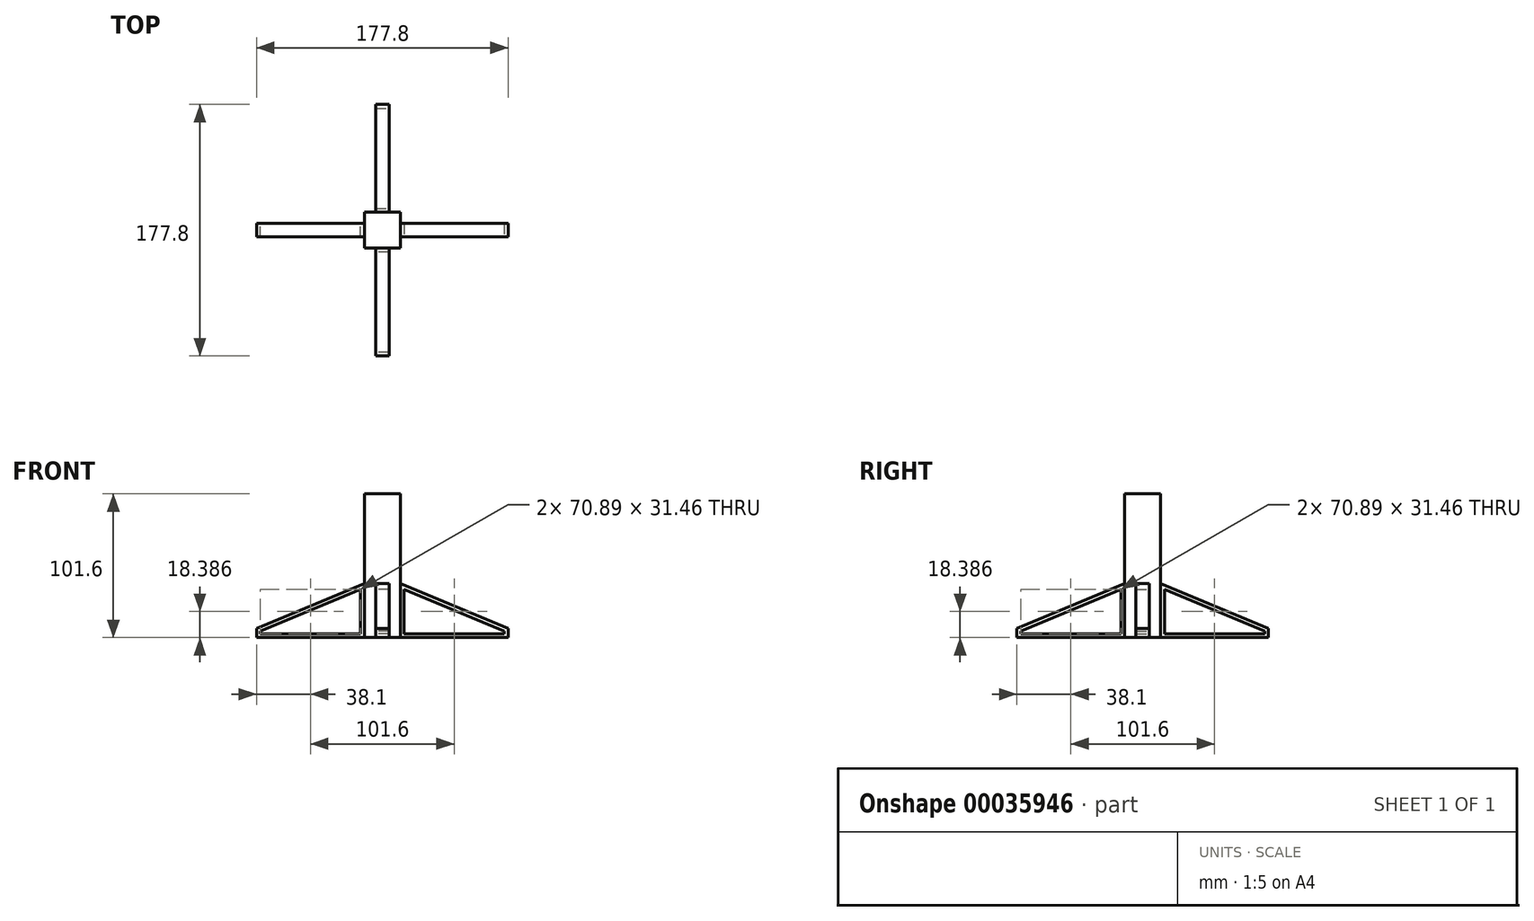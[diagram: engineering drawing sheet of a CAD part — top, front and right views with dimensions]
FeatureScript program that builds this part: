
annotation { "Feature Type Name" : "Feature", "Feature Type Description" : "" }
export const myFeature = defineFeature(function(context is Context, id is Id, definition is map)
    precondition{}
    {
        {
            var Q0;
            Q0=qCreatedBy(makeId("Top.planeOp"),FACE);
            var sketch = newSketch(context, id + "F0", { "sketchPlane" : qUnion([Q0])});
            skLineSegment(sketch, "E0.rect.bottom", {"start": v(12.7, 12.7) * mm, "end": v(-12.7, 12.7) * mm});
            skLineSegment(sketch, "E0.rect.top", {"start": v(12.7, -12.7) * mm, "end": v(-12.7, -12.7) * mm});
            skLineSegment(sketch, "E0.rect.left", {"start": v(12.7, 12.7) * mm, "end": v(12.7, -12.7) * mm});
            skLineSegment(sketch, "E0.rect.right", {"start": v(-12.7, 12.7) * mm, "end": v(-12.7, -12.7) * mm});
            skPoint(sketch, "E0.rect.middle", {"position": v(0, 0) * mm});
            skSolve(sketch);
        }
        {
            var Q0;
            Q0 = qSketchRegion(id + "F0", true);
            extrude(context, id + "F1", {"entities" : qUnion([Q0]), "oppositeDirection" : true, "depth" : 101.6 * mm});
        }
        {
            var Q0;
            Q0=qCreatedBy(makeId("Right.planeOp"),FACE);
            var sketch = newSketch(context, id + "F2", { "sketchPlane" : qUnion([Q0])});
            skLineSegment(sketch, "E1.0", {"start": v(-12.7, -101.6) * mm, "end": v(-12.7, -63.5) * mm});
            skLineSegment(sketch, "E2", {"start": v(-12.7, -101.6) * mm, "end": v(-88.9, -101.6) * mm});
            skLineSegment(sketch, "E3", {"start": v(-88.9, -101.6) * mm, "end": v(-88.9, -95.25) * mm});
            skLineSegment(sketch, "E4", {"start": v(-88.9, -95.25) * mm, "end": v(-12.7, -63.5) * mm});
            skPoint(sketch, "E5.orphan", {"position": v(-12.7, 0) * mm});
            skLineSegment(sketch, "E6.0", {"start": v(-15.36, -98.94) * mm, "end": v(-15.36, -67.49) * mm});
            skLineSegment(sketch, "E6.1", {"start": v(-15.36, -98.94) * mm, "end": v(-86.24, -98.94) * mm});
            skLineSegment(sketch, "E6.2", {"start": v(-86.24, -98.94) * mm, "end": v(-86.24, -97.02) * mm});
            skLineSegment(sketch, "E6.3", {"start": v(-86.24, -97.02) * mm, "end": v(-15.36, -67.49) * mm});
            skSolve(sketch);
        }
        {
            var Q0;
            {var subQ1=sQuery(id+"F2.wireOp",EDGE,"E2");Q0=makeQuery(id+"F2.imprint","IMPRINT",FACE,{"disambiguationData":[TD([[makeQuery(id+"F2.imprint","IMPRINT",EDGE,{"derivedFrom":subQ1}),-1.0]])]});}
            extrude(context, id + "F3", {"entities" : qUnion([Q0]), "endBound" : BoundingType.SYMMETRIC, "depth" : 9.52 * mm});
        }
        {
            var Q0;
            Q0=qCreatedBy(makeId("Front.planeOp"),FACE);
            var sketch = newSketch(context, id + "F4", { "sketchPlane" : qUnion([Q0])});
            skLineSegment(sketch, "E7", {"start": v(0, 0) * mm, "end": v(0, -105.5) * mm});
            skSolve(sketch);
        }
        {
            var Q0;
            Q0=makeQuery(id+"F3.opExtrude","SWEPT_BODY",BODY,{"disambiguationData":[OSD([sQuery(id+"F2.wireOp",EDGE,"E1.0"),sQuery(id+"F2.wireOp",EDGE,"E2"),sQuery(id+"F2.wireOp",EDGE,"E3"),sQuery(id+"F2.wireOp",EDGE,"E4")])]});
            var Q1;
            Q1=sQuery(id+"F4.wireOp",EDGE,"E7");
            circularPattern(context, id + "F5", {"entities" : qUnion([Q0]), "axis" : qUnion([Q1]), "angle" : 90 * degree, "instanceCount" : 4});
        }
    });
